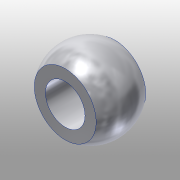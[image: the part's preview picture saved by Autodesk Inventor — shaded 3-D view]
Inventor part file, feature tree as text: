
AUTODESK INVENTOR PART (.ipt)
format: ipt  version: 2016 (Build 200138000, 138)  size: 133,120 bytes
history: native  units: mm
features: sketch x3, extrude x2, revolve x1
ambient origin geometry x8: Origin, YZ Plane, XZ Plane, XY Plane, X Axis, Y Axis, Z Axis, Center Point
bodies: Solid1 (feature_tree)
feature tree (6):
  revolve  "Revolution1"  Angle=90.0deg
  extrude  "Extrusion1"  Depth=10.0mm TaperAngle=0.0deg
  extrude  "Extrusion2"  Depth=10.0mm TaperAngle=0.0deg
  sketch  "Sketch1"  dims[d0=6.4mm d1=90.0deg]
  sketch  "Sketch2"  dims[d2=4.0mm d3=10.0mm d4=0.0mm]
  sketch  "Sketch3"  dims[d5=3.2mm d6=10.0mm d7=0.0mm]
